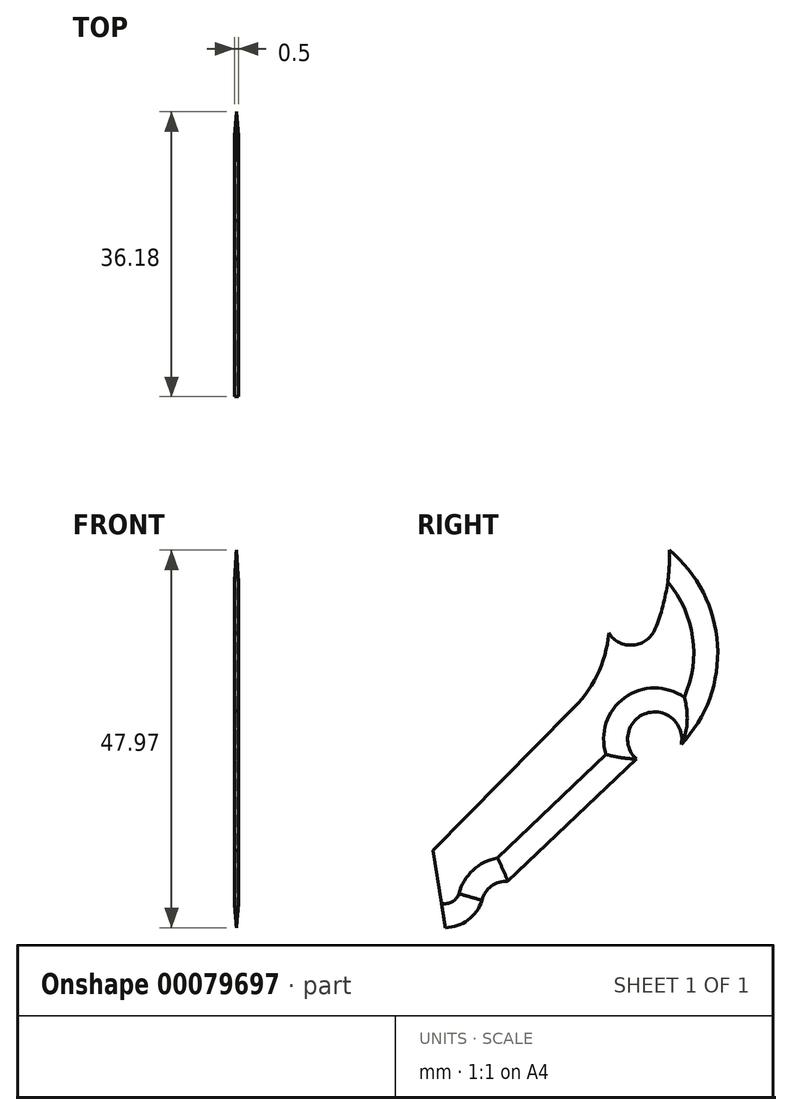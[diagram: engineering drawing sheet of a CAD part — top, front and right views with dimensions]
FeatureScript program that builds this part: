
annotation { "Feature Type Name" : "Feature", "Feature Type Description" : "" }
export const myFeature = defineFeature(function(context is Context, id is Id, definition is map)
    precondition{}
    {
        {
            var Q0;
            Q0=qCreatedBy(makeId("Right.planeOp"),FACE);
            var sketch = newSketch(context, id + "F0", { "sketchPlane" : qUnion([Q0])});
            skLineSegment(sketch, "E0", {"start": v(-5.9, -17.04) * mm, "end": v(10.42, -1.5) * mm});
            skArc(sketch, "E1", {"start": v(16.13, 0.32) * mm, "mid": v(11.72, 4.3) * mm, "end": v(10.42, -1.5) * mm});
            skArc(sketch, "E2", {"start": v(16.13, 0.32) * mm, "mid": v(20.74, 13) * mm, "end": v(14.63, 25.02) * mm});
            skArc(sketch, "E3", {"start": v(12.83, 15) * mm, "mid": v(14.25, 19.92) * mm, "end": v(14.63, 25.02) * mm});
            skArc(sketch, "E4", {"start": v(6.93, 14.47) * mm, "mid": v(10.04, 12.95) * mm, "end": v(12.83, 15) * mm});
            skArc(sketch, "E5", {"start": v(2.07, 4.6) * mm, "mid": v(5.43, 9.07) * mm, "end": v(6.93, 14.47) * mm});
            skLineSegment(sketch, "E6", {"start": v(2.07, 4.6) * mm, "end": v(-15.4, -13.13) * mm});
            skArc(sketch, "E7", {"start": v(-5.9, -17.04) * mm, "mid": v(-7.98, -17.65) * mm, "end": v(-9.16, -19.46) * mm});
            skArc(sketch, "E8", {"start": v(-13.83, -22.95) * mm, "mid": v(-10.93, -21.96) * mm, "end": v(-9.16, -19.46) * mm});
            skLineSegment(sketch, "E9", {"start": v(-15.4, -13.13) * mm, "end": v(-13.83, -22.95) * mm});
            skSolve(sketch);
        }
        {
            var Q0;
            Q0 = qSketchRegion(id + "F0", true);
            extrude(context, id + "F1", {"entities" : qUnion([Q0]), "endBound" : BoundingType.SYMMETRIC, "depth" : 0.5 * mm});
        }
        {
            var Q0;
            Q0=makeQuery(id+"F1.opExtrude","CAP_EDGE",EDGE,{"disambiguationData":[OSD([sQuery(id+"F0.wireOp",EDGE,"E7")])],"isStart":true});
            var Q1;
            Q1=makeQuery(id+"F1.opExtrude","CAP_EDGE",EDGE,{"disambiguationData":[OSD([sQuery(id+"F0.wireOp",EDGE,"E8")])],"isStart":true});
            var Q2;
            Q2=makeQuery(id+"F1.opExtrude","CAP_EDGE",EDGE,{"disambiguationData":[OSD([sQuery(id+"F0.wireOp",EDGE,"E0")])],"isStart":true});
            var Q3;
            Q3=makeQuery(id+"F1.opExtrude","CAP_EDGE",EDGE,{"disambiguationData":[OSD([sQuery(id+"F0.wireOp",EDGE,"E1")])],"isStart":true});
            var Q4;
            Q4=makeQuery(id+"F1.opExtrude","CAP_EDGE",EDGE,{"disambiguationData":[OSD([sQuery(id+"F0.wireOp",EDGE,"E2")])],"isStart":true});
            chamfer(context, id + "F2", {"entities" : qUnion([Q0, Q1, Q2, Q3, Q4]), "chamferType" : ChamferType.TWO_OFFSETS, "width1" : 3.05 * mm, "oppositeDirection" : false, "width2" : 0.25 * mm, "tangentPropagation" : true});
        }
        {
            var Q0;
            Q0=makeQuery(id+"F1.opExtrude","CAP_EDGE",EDGE,{"disambiguationData":[OSD([sQuery(id+"F0.wireOp",EDGE,"E2")])],"isStart":false});
            var Q1;
            Q1=makeQuery(id+"F1.opExtrude","CAP_EDGE",EDGE,{"disambiguationData":[OSD([sQuery(id+"F0.wireOp",EDGE,"E1")])],"isStart":false});
            var Q2;
            Q2=makeQuery(id+"F1.opExtrude","CAP_EDGE",EDGE,{"disambiguationData":[OSD([sQuery(id+"F0.wireOp",EDGE,"E0")])],"isStart":false});
            var Q3;
            Q3=makeQuery(id+"F1.opExtrude","CAP_EDGE",EDGE,{"disambiguationData":[OSD([sQuery(id+"F0.wireOp",EDGE,"E7")])],"isStart":false});
            var Q4;
            Q4=makeQuery(id+"F1.opExtrude","CAP_EDGE",EDGE,{"disambiguationData":[OSD([sQuery(id+"F0.wireOp",EDGE,"E8")])],"isStart":false});
            chamfer(context, id + "F3", {"entities" : qUnion([Q0, Q1, Q2, Q3, Q4]), "chamferType" : ChamferType.TWO_OFFSETS, "width1" : 3.05 * mm, "oppositeDirection" : false, "width2" : 0.25 * mm, "tangentPropagation" : true});
        }
    });
